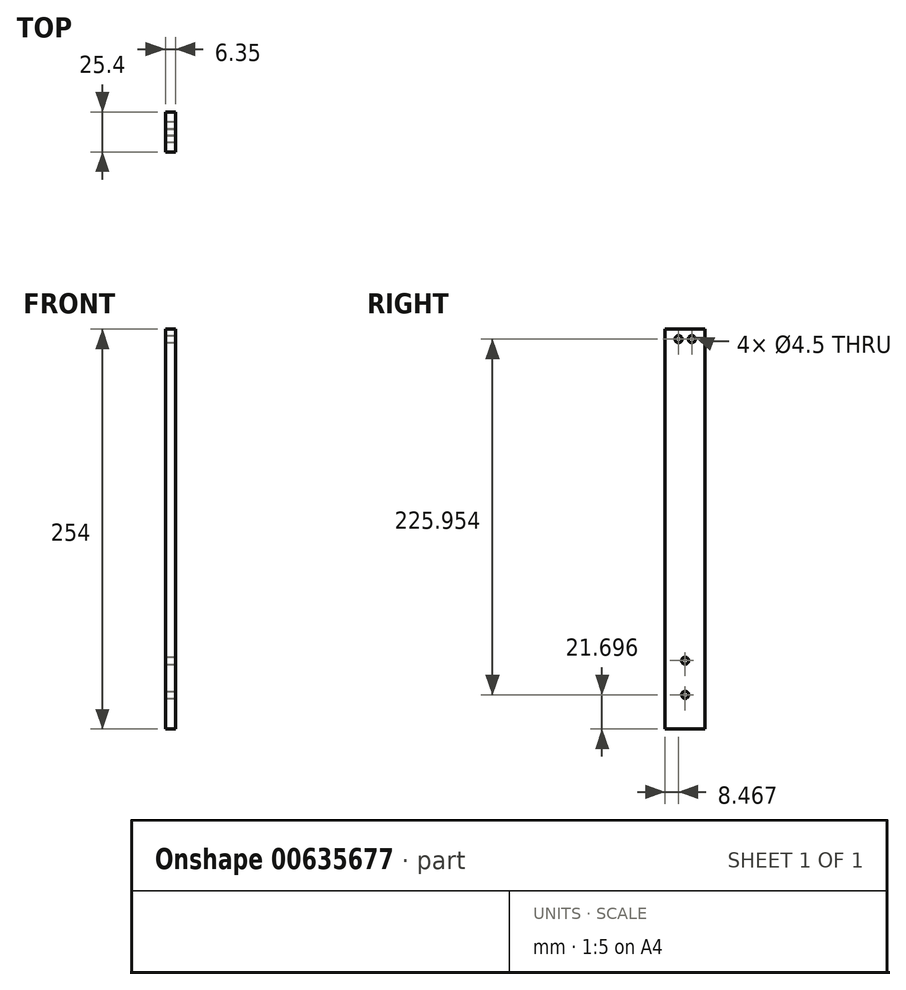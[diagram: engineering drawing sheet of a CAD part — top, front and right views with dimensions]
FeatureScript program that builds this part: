
annotation { "Feature Type Name" : "Feature", "Feature Type Description" : "" }
export const myFeature = defineFeature(function(context is Context, id is Id, definition is map)
    precondition{}
    {
        {
            var Q0;
            Q0=qCreatedBy(makeId("Right.planeOp"),FACE);
            var sketch = newSketch(context, id + "F0", { "sketchPlane" : qUnion([Q0])});
            skLineSegment(sketch, "E0.bottom", {"start": v(0, 0) * mm, "end": v(25.4, 0) * mm});
            skLineSegment(sketch, "E0.top", {"start": v(0, 254) * mm, "end": v(25.4, 254) * mm});
            skLineSegment(sketch, "E0.left", {"start": v(0, 0) * mm, "end": v(0, 254) * mm});
            skLineSegment(sketch, "E0.right", {"start": v(25.4, 0) * mm, "end": v(25.4, 254) * mm});
            skSolve(sketch);
        }
        {
            var Q0;
            Q0 = qSketchRegion(id + "F0", true);
            extrude(context, id + "F1", {"entities" : qUnion([Q0]), "oppositeDirection" : true, "depth" : 6.35 * mm, "offsetDistance" : 25.4 * mm});
        }
        {
            var Q0;
            Q0=makeQuery(id+"F1.opExtrude","CAP_FACE",FACE,{"disambiguationData":[OSD([sQuery(id+"F0.wireOp",EDGE,"E0.bottom"),sQuery(id+"F0.wireOp",EDGE,"E0.top"),sQuery(id+"F0.wireOp",EDGE,"E0.left"),sQuery(id+"F0.wireOp",EDGE,"E0.right")])],"isStart":true});
            var sketch = newSketch(context, id + "F2", { "sketchPlane" : qUnion([Q0])});
            skLineSegment(sketch, "E1", {"start": v(0, 247.65) * mm, "end": v(25.4, 247.65) * mm, "construction": true});
            skPoint(sketch, "E2", {"position": v(8.47, 247.65) * mm});
            skPoint(sketch, "E3", {"position": v(16.93, 247.65) * mm});
            skSolve(sketch);
        }
        {
            var Q0;
            Q0=sQuery(id+"F2.wireOp",VERTEX,"E2");
            var Q1;
            Q1=sQuery(id+"F2.wireOp",VERTEX,"E3");
            var Q2;
            Q2=makeQuery(id+"F1.opExtrude","SWEPT_BODY",BODY,{"disambiguationData":[OSD([sQuery(id+"F0.wireOp",EDGE,"E0.bottom"),sQuery(id+"F0.wireOp",EDGE,"E0.top"),sQuery(id+"F0.wireOp",EDGE,"E0.left"),sQuery(id+"F0.wireOp",EDGE,"E0.right")])]});
            hole(context, id + "F3", {"style" : HoleStyle.SIMPLE, "endStyle" : HoleEndStyle.THROUGH, "standardTappedOrClearance" : lookupTablePath({ "standard" : "ANSI", "fit" : "Normal (ASME)", "size" : "#8", "type" : "Clearance" }), "standardBlindInLast" : lookupTablePath({ "fit" : "Free", "standard" : "ANSI", "size" : "#8", "type" : "Clearance" }), "holeDiameter" : 4.5 * mm, "majorDiameter" : 3.5 * mm, "isTappedThrough" : true, "tappedDepth" : 12.85 * mm, "tapClearance" : 3, "locations" : qUnion([Q0, Q1]), "scope" : qUnion([Q2])});
        }
        {
            var Q0;
            Q0=makeQuery(id+"F1.opExtrude","CAP_FACE",FACE,{"disambiguationData":[OSD([sQuery(id+"F0.wireOp",EDGE,"E0.bottom"),sQuery(id+"F0.wireOp",EDGE,"E0.top"),sQuery(id+"F0.wireOp",EDGE,"E0.left"),sQuery(id+"F0.wireOp",EDGE,"E0.right")])],"isStart":true});
            var sketch = newSketch(context, id + "F4", { "sketchPlane" : qUnion([Q0])});
            skLineSegment(sketch, "E4", {"start": v(12.7, 0) * mm, "end": v(12.7, 254) * mm, "construction": true});
            skPoint(sketch, "E5", {"position": v(12.7, 21.7) * mm});
            skPoint(sketch, "E6", {"position": v(12.7, 43.4) * mm});
            skLineSegment(sketch, "E7", {"start": v(0, 65.09) * mm, "end": v(25.4, 65.09) * mm, "construction": true});
            skSolve(sketch);
        }
        {
            var Q0;
            Q0=sQuery(id+"F4.wireOp",VERTEX,"E6");
            var Q1;
            Q1=sQuery(id+"F4.wireOp",VERTEX,"E5");
            var Q2;
            Q2=makeQuery(id+"F1.opExtrude","SWEPT_BODY",BODY,{"disambiguationData":[OSD([sQuery(id+"F0.wireOp",EDGE,"E0.bottom"),sQuery(id+"F0.wireOp",EDGE,"E0.top"),sQuery(id+"F0.wireOp",EDGE,"E0.left"),sQuery(id+"F0.wireOp",EDGE,"E0.right")])]});
            hole(context, id + "F5", {"style" : HoleStyle.SIMPLE, "endStyle" : HoleEndStyle.THROUGH, "standardTappedOrClearance" : lookupTablePath({ "standard" : "ANSI", "fit" : "Normal (ASME)", "size" : "#8", "type" : "Clearance" }), "standardBlindInLast" : lookupTablePath({ "fit" : "Free", "standard" : "ANSI", "size" : "#8", "type" : "Clearance" }), "holeDiameter" : 4.5 * mm, "majorDiameter" : 6.35 * mm, "isTappedThrough" : true, "tappedDepth" : 12.85 * mm, "tapClearance" : 3, "locations" : qUnion([Q0, Q1]), "scope" : qUnion([Q2])});
        }
    });
